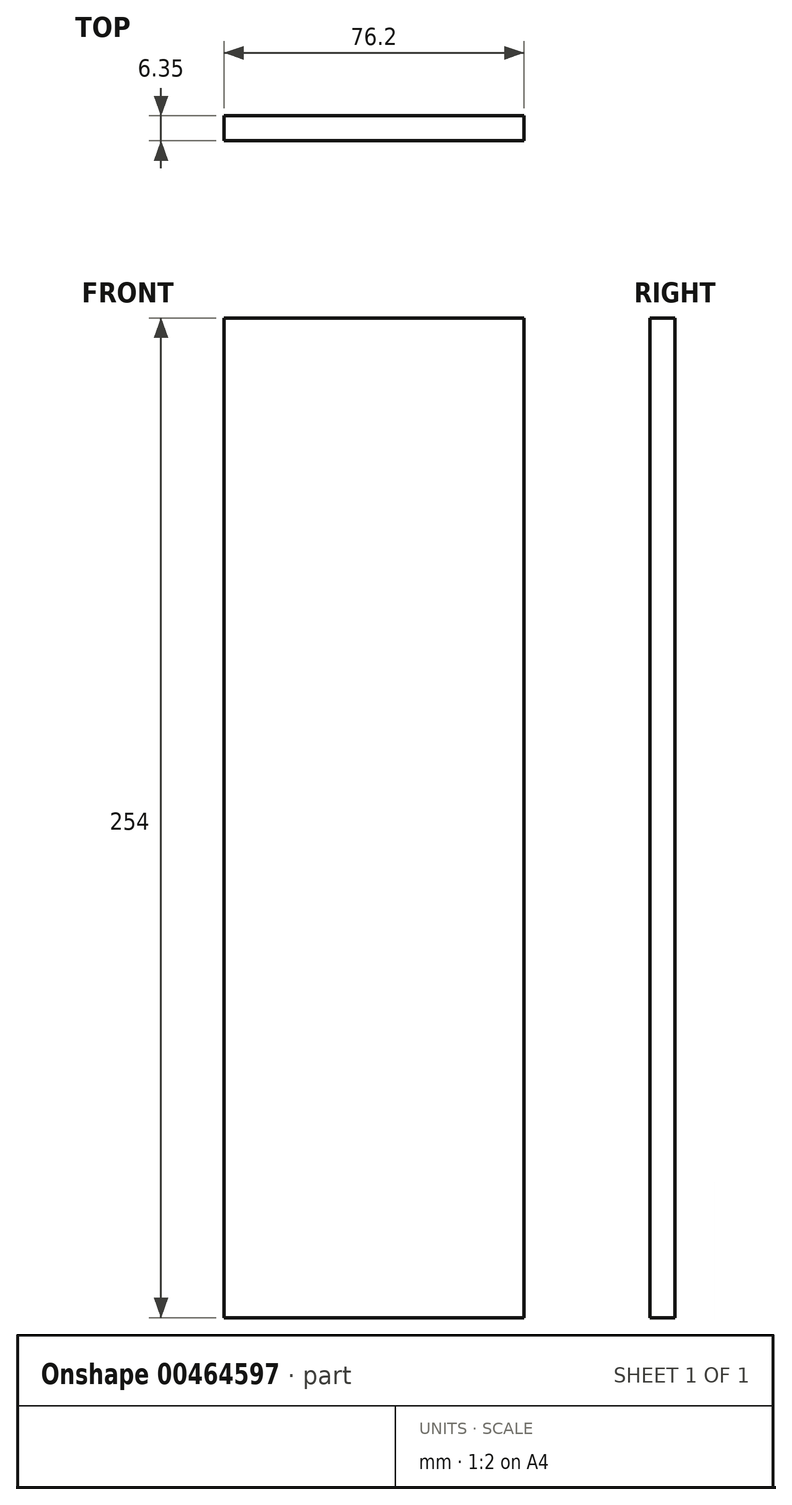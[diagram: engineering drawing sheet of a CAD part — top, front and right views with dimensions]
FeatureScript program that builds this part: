
annotation { "Feature Type Name" : "Feature", "Feature Type Description" : "" }
export const myFeature = defineFeature(function(context is Context, id is Id, definition is map)
    precondition{}
    {
        {
            var Q0;
            Q0=qCreatedBy(makeId("Front.planeOp"),FACE);
            var sketch = newSketch(context, id + "F0", { "sketchPlane" : qUnion([Q0])});
            skLineSegment(sketch, "E0.bottom", {"start": v(-63.75, 203.25) * mm, "end": v(12.45, 203.25) * mm});
            skLineSegment(sketch, "E0.top", {"start": v(-63.75, -50.75) * mm, "end": v(12.45, -50.75) * mm});
            skLineSegment(sketch, "E0.left", {"start": v(-63.75, 203.25) * mm, "end": v(-63.75, -50.75) * mm});
            skLineSegment(sketch, "E0.right", {"start": v(12.45, 203.25) * mm, "end": v(12.45, -50.75) * mm});
            skSolve(sketch);
        }
        {
            var Q0;
            Q0 = qSketchRegion(id + "F0", true);
            extrude(context, id + "F1", {"entities" : qUnion([Q0]), "depth" : 6.35 * mm});
        }
    });
